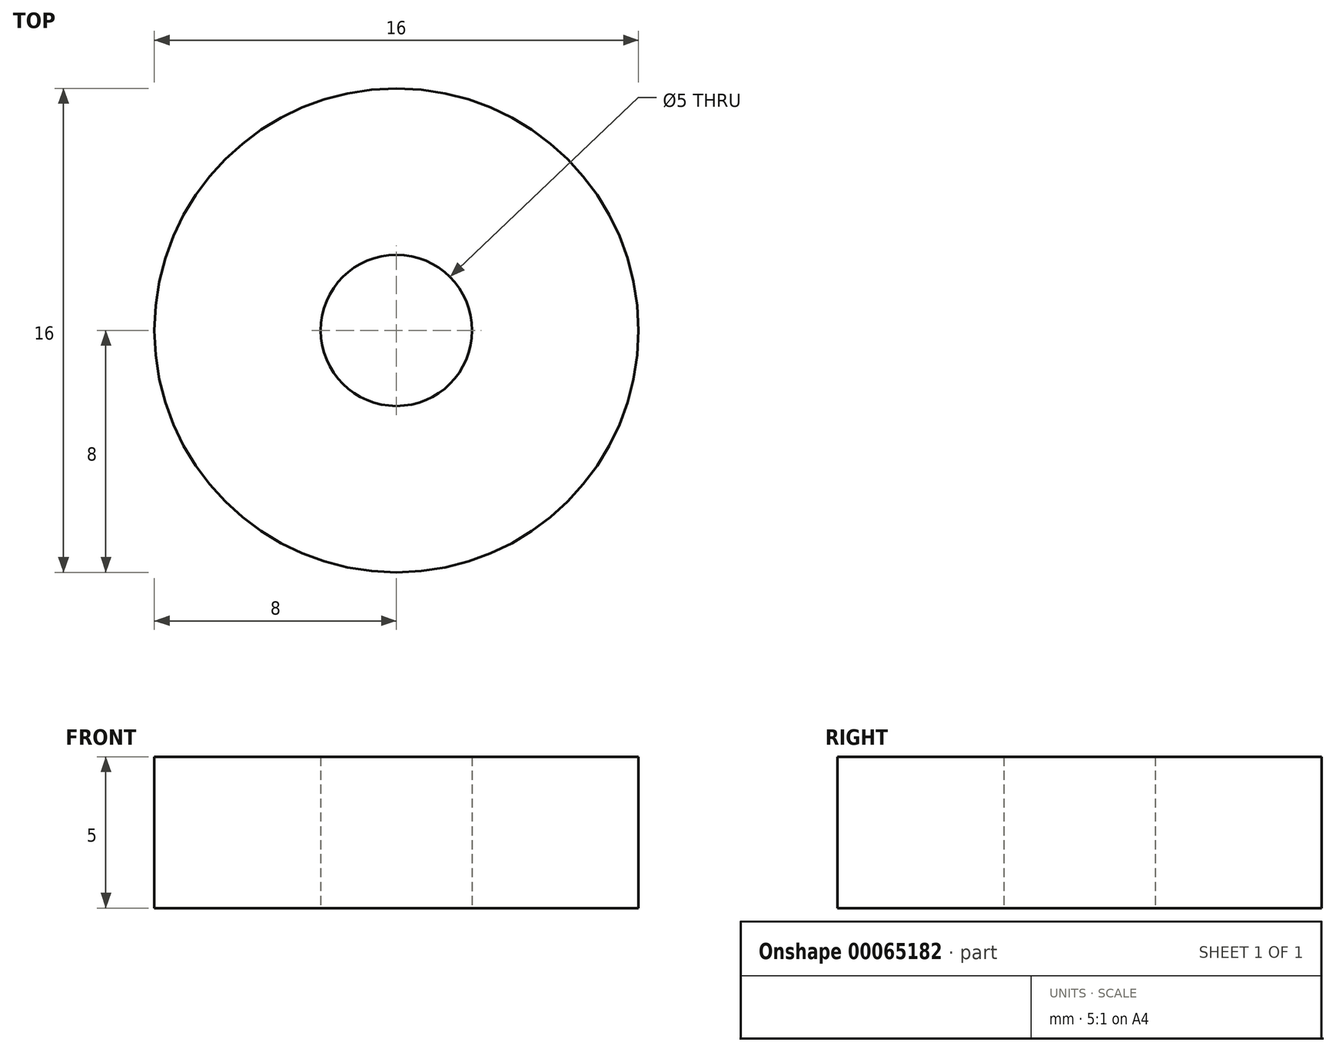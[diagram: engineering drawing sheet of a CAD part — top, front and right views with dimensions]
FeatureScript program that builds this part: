
annotation { "Feature Type Name" : "Feature", "Feature Type Description" : "" }
export const myFeature = defineFeature(function(context is Context, id is Id, definition is map)
    precondition{}
    {
        {
            var Q0;
            Q0=qCreatedBy(makeId("Top.planeOp"),FACE);
            var sketch = newSketch(context, id + "F0", { "sketchPlane" : qUnion([Q0])});
            skCircle(sketch, "E0", {"center": v(0, 0) * mm, "radius": 8 * mm});
            skCircle(sketch, "E1", {"center": v(0, 0) * mm, "radius": 2.5 * mm});
            skSolve(sketch);
        }
        {
            var Q0;
            Q0 = qSketchRegion(id + "F0", true);
            extrude(context, id + "F1", {"entities" : qUnion([Q0]), "depth" : 5 * mm});
        }
    });
